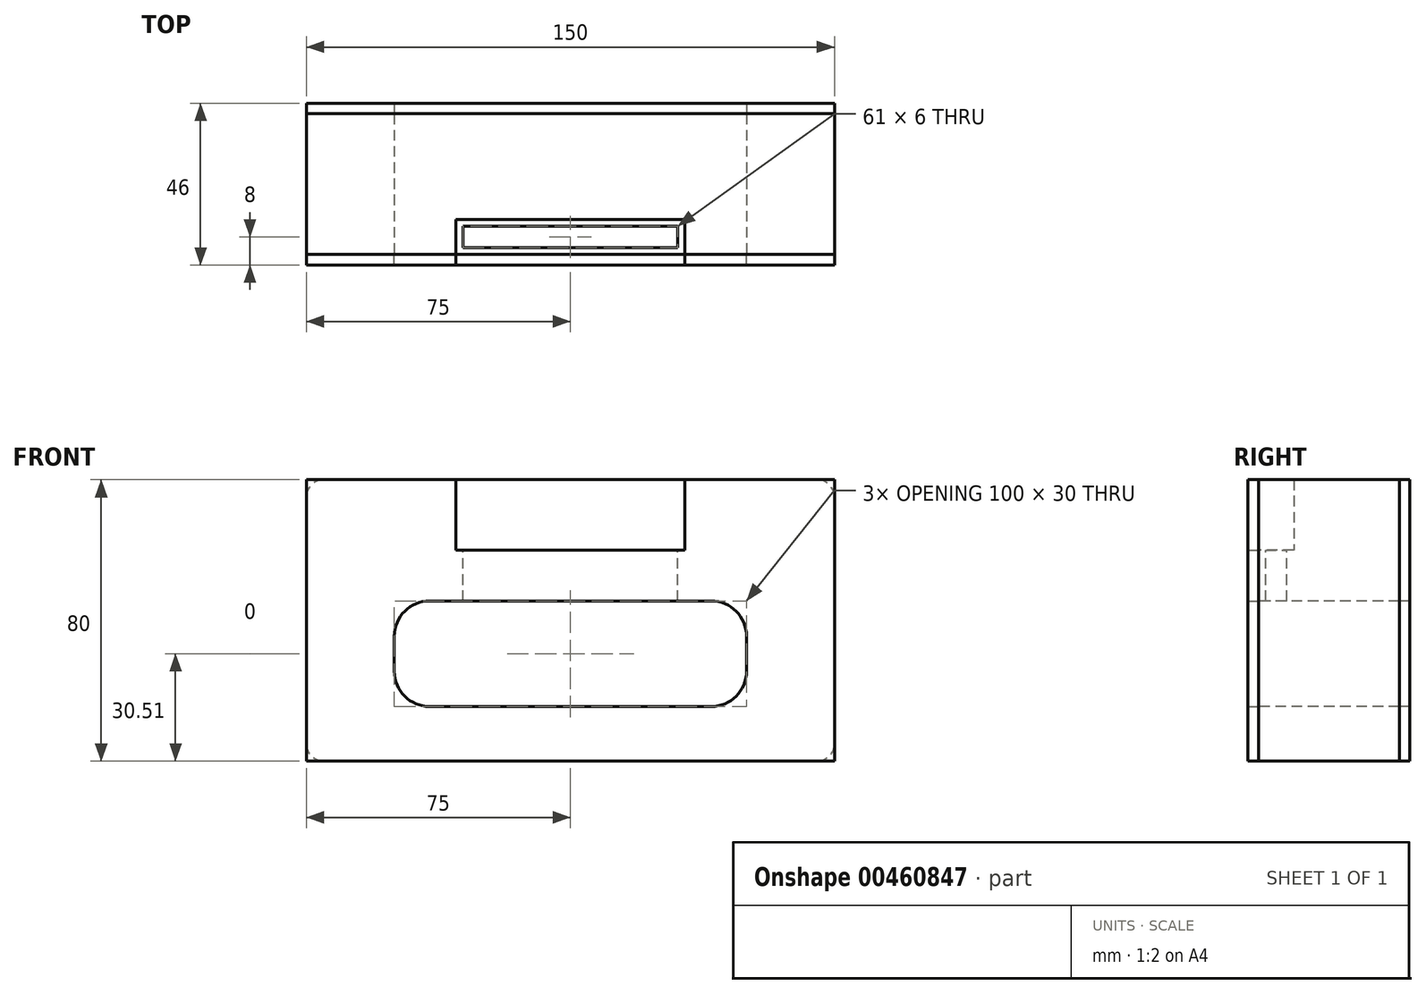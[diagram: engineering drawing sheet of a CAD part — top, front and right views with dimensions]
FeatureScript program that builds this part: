
annotation { "Feature Type Name" : "Feature", "Feature Type Description" : "" }
export const myFeature = defineFeature(function(context is Context, id is Id, definition is map)
    precondition{}
    {
        {
            var Q0;
            Q0=qCreatedBy(makeId("Top.planeOp"),FACE);
            var sketch = newSketch(context, id + "F0", { "sketchPlane" : qUnion([Q0])});
            skLineSegment(sketch, "E0.bottom", {"start": v(-75, 20) * mm, "end": v(75, 20) * mm});
            skLineSegment(sketch, "E0.top", {"start": v(-75, -20) * mm, "end": v(75, -20) * mm});
            skLineSegment(sketch, "E0.left", {"start": v(-75, 20) * mm, "end": v(-75, -20) * mm});
            skLineSegment(sketch, "E0.right", {"start": v(75, 20) * mm, "end": v(75, -20) * mm});
            skPoint(sketch, "E0.middle", {"position": v(0, 0) * mm});
            skSolve(sketch);
        }
        {
            var Q0;
            Q0 = qSketchRegion(id + "F0", true);
            extrude(context, id + "F1", {"entities" : qUnion([Q0]), "depth" : 80 * mm});
        }
        {
            var Q0;
            Q0=makeQuery(id+"F1.opExtrude","SWEPT_FACE",FACE,{"disambiguationData":[OSD([sQuery(id+"F0.wireOp",EDGE,"E0.top")])]});
            var sketch = newSketch(context, id + "F2", { "sketchPlane" : qUnion([Q0])});
            skLineSegment(sketch, "E1.bottom", {"start": v(-32.5, 80) * mm, "end": v(32.5, 80) * mm});
            skLineSegment(sketch, "E1.top", {"start": v(-32.5, 60) * mm, "end": v(32.5, 60) * mm});
            skLineSegment(sketch, "E1.left", {"start": v(-32.5, 80) * mm, "end": v(-32.5, 60) * mm});
            skLineSegment(sketch, "E1.right", {"start": v(32.5, 80) * mm, "end": v(32.5, 60) * mm});
            skSolve(sketch);
        }
        {
            var Q0;
            Q0=makeQuery(id+"F2.imprint","IMPRINT",FACE,{"disambiguationData":[TD([[makeQuery(id+"F2.imprint","IMPRINT",EDGE,{"derivedFrom":sQuery(id+"F2.wireOp",EDGE,"E1.bottom")}),-1.0]])]});
            extrude(context, id + "F3", {"entities" : qUnion([Q0]), "operationType" : NewBodyOperationType.REMOVE, "oppositeDirection" : true, "depth" : 10 * mm});
        }
        {
            var Q0;
            Q0=makeQuery(id+"F1.opExtrude","SWEPT_FACE",FACE,{"disambiguationData":[OSD([sQuery(id+"F0.wireOp",EDGE,"E0.top")])]});
            var sketch = newSketch(context, id + "F4", { "sketchPlane" : qUnion([Q0])});
            skLineSegment(sketch, "E2.bottom", {"start": v(-40, 45.5) * mm, "end": v(40, 45.5) * mm});
            skLineSegment(sketch, "E2.top", {"start": v(-40, 15.5) * mm, "end": v(40, 15.5) * mm});
            skLineSegment(sketch, "E2.left", {"start": v(-50, 35.5) * mm, "end": v(-50, 25.5) * mm});
            skLineSegment(sketch, "E2.right", {"start": v(50, 35.5) * mm, "end": v(50, 25.5) * mm});
            skPoint(sketch, "E3.visualSharp", {"position": v(-50, 45.5) * mm});
            skArc(sketch, "E3.filletArc", {"start": v(-40, 45.5) * mm, "mid": v(-47.07, 42.58) * mm, "end": v(-50, 35.5) * mm});
            skPoint(sketch, "E4.visualSharp", {"position": v(-50, 15.5) * mm});
            skArc(sketch, "E4.filletArc", {"start": v(-50, 25.5) * mm, "mid": v(-47.07, 18.44) * mm, "end": v(-40, 15.5) * mm});
            skPoint(sketch, "E5.visualSharp", {"position": v(50, 15.5) * mm});
            skArc(sketch, "E5.filletArc", {"start": v(40, 15.5) * mm, "mid": v(47.07, 18.44) * mm, "end": v(50, 25.5) * mm});
            skPoint(sketch, "E6.visualSharp", {"position": v(50, 45.5) * mm});
            skArc(sketch, "E6.filletArc", {"start": v(50, 35.5) * mm, "mid": v(47.07, 42.58) * mm, "end": v(40, 45.5) * mm});
            skSolve(sketch);
        }
        {
            var Q0;
            Q0 = qSketchRegion(id + "F4", true);
            extrude(context, id + "F5", {"entities" : qUnion([Q0]), "operationType" : NewBodyOperationType.REMOVE, "oppositeDirection" : true, "depth" : 153.5 * mm});
        }
        {
            var Q0;
            Q0=makeQuery(id+"F3.boolean.opBoolean","COPY",FACE,{"derivedFrom":makeQuery(id+"F3.opExtrude","SWEPT_FACE",FACE,{"disambiguationData":[OSD([sQuery(id+"F2.wireOp",EDGE,"E1.top")])]})});
            var sketch = newSketch(context, id + "F6", { "sketchPlane" : qUnion([Q0])});
            skLineSegment(sketch, "E7.bottom", {"start": v(-30.5, -18) * mm, "end": v(30.5, -18) * mm});
            skLineSegment(sketch, "E7.top", {"start": v(-30.5, -12) * mm, "end": v(30.5, -12) * mm});
            skLineSegment(sketch, "E7.left", {"start": v(-30.5, -18) * mm, "end": v(-30.5, -12) * mm});
            skLineSegment(sketch, "E7.right", {"start": v(30.5, -18) * mm, "end": v(30.5, -12) * mm});
            skSolve(sketch);
        }
        {
            var Q0;
            Q0 = qSketchRegion(id + "F6", true);
            extrude(context, id + "F7", {"entities" : qUnion([Q0]), "operationType" : NewBodyOperationType.REMOVE, "oppositeDirection" : true, "depth" : 36.1 * mm});
        }
        {
            var Q0;
            Q0 = qSketchRegion(id + "F6", true);
            extrude(context, id + "F8", {"entities" : qUnion([Q0]), "operationType" : NewBodyOperationType.REMOVE, "oppositeDirection" : true, "depth" : 39.9 * mm});
        }
        {
            var Q0;
            Q0=makeQuery(id+"F1.opExtrude","SWEPT_FACE",FACE,{"disambiguationData":[OSD([sQuery(id+"F0.wireOp",EDGE,"E0.top")])]});
            var sketch = newSketch(context, id + "F9", { "sketchPlane" : qUnion([Q0])});
            skPoint(sketch, "E8.0", {"position": v(40, 45.5) * mm});
            skArc(sketch, "E9.0", {"start": v(50, 35.5) * mm, "mid": v(47.07, 42.58) * mm, "end": v(40, 45.5) * mm});
            skLineSegment(sketch, "E10.0", {"start": v(50, 35.5) * mm, "end": v(50, 25.5) * mm});
            skArc(sketch, "E11.0", {"start": v(40, 15.5) * mm, "mid": v(47.07, 18.44) * mm, "end": v(50, 25.5) * mm});
            skLineSegment(sketch, "E12.0", {"start": v(-40, 15.5) * mm, "end": v(40, 15.5) * mm});
            skLineSegment(sketch, "E13.0", {"start": v(-40, 45.5) * mm, "end": v(40, 45.5) * mm});
            skArc(sketch, "E14.0", {"start": v(-40, 45.5) * mm, "mid": v(-47.07, 42.58) * mm, "end": v(-50, 35.5) * mm});
            skArc(sketch, "E15.0", {"start": v(-50, 25.5) * mm, "mid": v(-47.07, 18.44) * mm, "end": v(-40, 15.5) * mm});
            skPoint(sketch, "E16.0", {"position": v(-50, 30.5) * mm});
            skLineSegment(sketch, "E17.0", {"start": v(-50, 35.5) * mm, "end": v(-50, 25.5) * mm});
            skSolve(sketch);
        }
        {
            var Q0;
            Q0=makeQuery(id+"F9.imprint","IMPRINT",FACE,{"disambiguationData":[TD([[makeQuery(id+"F9.imprint","IMPRINT",EDGE,{"derivedFrom":sQuery(id+"F9.wireOp",EDGE,"E9.0")}),-1.0]])]});
            extrude(context, id + "F10", {"entities" : qUnion([Q0]), "depth" : 3 * mm});
        }
        {
            var Q0;
            Q0=makeQuery(id+"F1.opExtrude","SWEPT_FACE",FACE,{"disambiguationData":[OSD([sQuery(id+"F0.wireOp",EDGE,"E0.bottom")])]});
            extrude(context, id + "F11", {"entities" : qUnion([Q0]), "depth" : 3 * mm});
        }
        {
            var Q0;
            Q0=makeQuery(id+"F1.opExtrude","SWEPT_FACE",FACE,{"disambiguationData":[OSD([sQuery(id+"F0.wireOp",EDGE,"E0.bottom")])]});
            var sketch = newSketch(context, id + "F12", { "sketchPlane" : qUnion([Q0])});
            skLineSegment(sketch, "E18.bottom", {"start": v(75, 80) * mm, "end": v(-75, 80) * mm});
            skLineSegment(sketch, "E18.top", {"start": v(75, 0) * mm, "end": v(-75, 0) * mm});
            skLineSegment(sketch, "E18.left", {"start": v(75, 80) * mm, "end": v(75, 0) * mm});
            skLineSegment(sketch, "E18.right", {"start": v(-75, 80) * mm, "end": v(-75, 0) * mm});
            skSolve(sketch);
        }
        {
            var Q0;
            Q0 = qSketchRegion(id + "F12", true);
            extrude(context, id + "F13", {"entities" : qUnion([Q0]), "depth" : 3 * mm});
        }
        {
            var Q0;
            Q0=makeQuery(id+"F1.opExtrude","CAP_EDGE",EDGE,{"disambiguationData":[OSD([sQuery(id+"F0.wireOp",EDGE,"E0.left")])],"isStart":false});
            fillet(context, id + "F14", {"entities" : qUnion([Q0]), "radius" : 5 * mm, "tangentPropagation" : true, "allowEdgeOverflow" : false});
        }
        {
            var Q0;
            Q0=makeQuery(id+"F1.opExtrude","CAP_EDGE",EDGE,{"disambiguationData":[OSD([sQuery(id+"F0.wireOp",EDGE,"E0.right")])],"isStart":false});
            fillet(context, id + "F15", {"entities" : qUnion([Q0]), "radius" : 5 * mm, "tangentPropagation" : true, "allowEdgeOverflow" : false});
        }
        {
            var Q0;
            Q0=makeQuery(id+"F1.opExtrude","CAP_EDGE",EDGE,{"disambiguationData":[OSD([sQuery(id+"F0.wireOp",EDGE,"E0.left")])],"isStart":true});
            fillet(context, id + "F16", {"entities" : qUnion([Q0]), "radius" : 5 * mm, "tangentPropagation" : true, "allowEdgeOverflow" : false});
        }
        {
            var Q0;
            Q0=makeQuery(id+"F1.opExtrude","CAP_EDGE",EDGE,{"disambiguationData":[OSD([sQuery(id+"F0.wireOp",EDGE,"E0.right")])],"isStart":true});
            fillet(context, id + "F17", {"entities" : qUnion([Q0]), "radius" : 5 * mm, "tangentPropagation" : true, "allowEdgeOverflow" : false});
        }
    });
